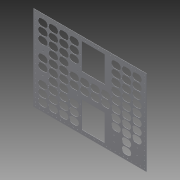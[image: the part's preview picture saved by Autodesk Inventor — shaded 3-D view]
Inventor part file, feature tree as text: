
AUTODESK INVENTOR PART (.ipt)
format: ipt  version: 2014 SP1 (Build 180222100, 222)  size: 957,952 bytes
history: native  units: in
note: dims shown in document units (in); Inventor stores cm internally (conversion verified against a paired STEP export)
features: reference x81, other x6, sketch x5, pattern_linear x2, sheet_metal_op x1, projected_geometry x1
ambient origin geometry x8: Origin, YZ Plane, XZ Plane, XY Plane, X Axis, Y Axis, Z Axis, Center Point
bodies: Solid1 (feature_tree)
feature tree (96):
  sheet_metal_op  "Face1"
  pattern_linear  "Rectangular Pattern2"  Spacing1=7.25in  [1 undecoded]
  pattern_linear  "Rectangular Pattern5"  Spacing1=0.0625in  [1 undecoded]
  sketch  "Sketch1"  dims[d0=27.0in]
  other  "Plate1"
  sketch  "Sketch2"  dims[d1=20.325in]
  sketch  "Sketch4"  dims[d2=0.0625in]
  reference  "Reference4"
  reference  "Reference5"
  sketch  "Sketch12"  dims[d4=7.25in]
  reference  "Reference10"
  reference  "Reference11"
  sketch  "Sketch16"  dims[d5=5.5in d6=7.25in d17=0.0625in d18=0.0in d19=10.6299in d21=1.0in d23=1.0in d24=1.0in d65=0.0625in d66=0.0in d78=11.55in d79=5.5in d80=11.55in d97=0.0625in d98=0.0in d99=7.4803in d101=1.0in d102=0.7874in d104=26.0in d105=0.0625in d106=0.0in d107=1.0in d109=1.8325in d110=2.5in d111=0.125in d112=3.937in d114=1.8325in d115=3.937in d117=2.5in d120=0.0625in d121=0.0in]
  reference  "Reference12"
  reference  "Reference13"
  reference  "Reference14"
  reference  "Reference15"
  reference  "Reference16"
  reference  "Reference17"
  reference  "Reference18"
  reference  "Reference19"
  reference  "Reference20"
  reference  "Reference21"
  reference  "Reference22"
  reference  "Reference23"
  reference  "Reference24"
  reference  "Reference25"
  reference  "Reference26"
  reference  "Reference27"
  reference  "Reference28"
  reference  "Reference29"
  reference  "Reference30"
  reference  "Reference31"
  reference  "Reference32"
  reference  "Reference33"
  reference  "Reference34"
  reference  "Reference35"
  reference  "Reference36"
  reference  "Reference37"
  reference  "Reference38"
  reference  "Reference39"
  reference  "Reference40"
  reference  "Reference41"
  reference  "Reference42"
  reference  "Reference43"
  reference  "Reference44"
  reference  "Reference45"
  reference  "Reference46"
  projected_geometry  "Projected Loop1"
  reference  "Reference47"
  reference  "Reference48"
  reference  "Reference49"
  reference  "Reference50"
  reference  "Reference51"
  reference  "Reference52"
  reference  "Reference53"
  reference  "Reference54"
  reference  "Reference55"
  reference  "Reference56"
  reference  "Reference57"
  reference  "Reference58"
  reference  "Reference59"
  reference  "Reference60"
  reference  "Reference61"
  reference  "Reference62"
  reference  "Reference63"
  reference  "Reference64"
  reference  "Reference65"
  reference  "Reference66"
  reference  "Reference67"
  reference  "Reference68"
  reference  "Reference69"
  reference  "Reference70"
  reference  "Reference71"
  reference  "Reference72"
  reference  "Reference73"
  reference  "Reference74"
  reference  "Reference75"
  reference  "Reference76"
  reference  "Reference77"
  reference  "Reference78"
  reference  "Reference79"
  reference  "Reference80"
  reference  "Reference81"
  reference  "Reference82"
  reference  "Reference83"
  reference  "Reference84"
  reference  "Reference85"
  reference  "Reference86"
  reference  "Reference87"
  reference  "Reference88"
  other  "Cut3"
  other  "Cut6"
  other  "Cut8"
  other  "Cut9"
  other  "Cut10"
note: 2 required parameter values undecoded (feature->parameter linkage not recoverable at this tier; creation-order binding heuristic only, values carry confidence <= 0.55)
